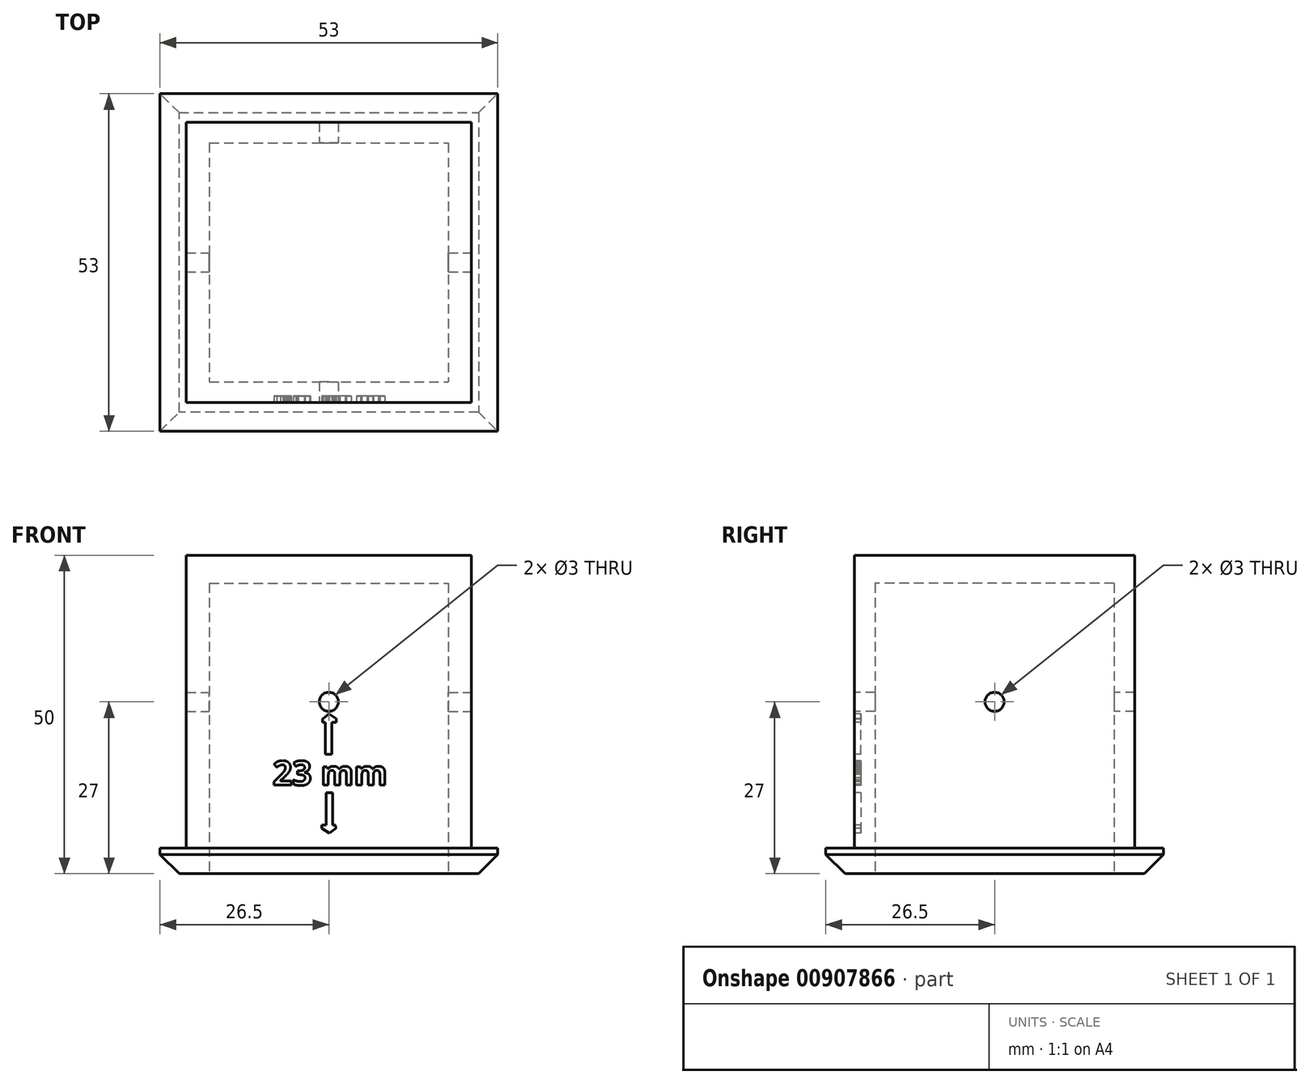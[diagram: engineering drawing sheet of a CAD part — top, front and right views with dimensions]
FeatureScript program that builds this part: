
annotation { "Feature Type Name" : "Feature", "Feature Type Description" : "" }
export const myFeature = defineFeature(function(context is Context, id is Id, definition is map)
    precondition{}
    {
        {
            var Q0;
            Q0=qCreatedBy(makeId("Top.planeOp"),FACE);
            var sketch = newSketch(context, id + "F0", { "sketchPlane" : qUnion([Q0])});
            skLineSegment(sketch, "E0.bottom", {"start": v(-18.75, 18.75) * mm, "end": v(18.75, 18.75) * mm});
            skLineSegment(sketch, "E0.top", {"start": v(-18.75, -18.75) * mm, "end": v(18.75, -18.75) * mm});
            skLineSegment(sketch, "E0.left", {"start": v(-18.75, 18.75) * mm, "end": v(-18.75, -18.75) * mm});
            skLineSegment(sketch, "E0.right", {"start": v(18.75, 18.75) * mm, "end": v(18.75, -18.75) * mm});
            skLineSegment(sketch, "E1.bottom", {"start": v(-22.4, 22) * mm, "end": v(22.4, 22) * mm});
            skLineSegment(sketch, "E1.top", {"start": v(-22.4, -22) * mm, "end": v(22.4, -22) * mm});
            skLineSegment(sketch, "E1.left", {"start": v(-22.4, 22) * mm, "end": v(-22.4, -22) * mm});
            skLineSegment(sketch, "E1.right", {"start": v(22.4, 22) * mm, "end": v(22.4, -22) * mm});
            skLineSegment(sketch, "E2", {"start": v(0, 18.75) * mm, "end": v(0, -18.75) * mm, "construction": true});
            skLineSegment(sketch, "E3", {"start": v(-18.75, 0) * mm, "end": v(18.75, 0) * mm, "construction": true});
            skLineSegment(sketch, "E4", {"start": v(0, 22) * mm, "end": v(0, -22) * mm, "construction": true});
            skLineSegment(sketch, "E5", {"start": v(-22.4, 0) * mm, "end": v(22.4, 0) * mm, "construction": true});
            skSolve(sketch);
        }
        {
            var Q0;
            Q0=makeQuery(id+"F0.imprint","IMPRINT",FACE,{"disambiguationData":[TD([[makeQuery(id+"F0.imprint","IMPRINT",EDGE,{"derivedFrom":sQuery(id+"F0.wireOp",EDGE,"E0.bottom")}),1.0]])]});
            var Q1;
            Q1=makeQuery(id+"F0.imprint","IMPRINT",FACE,{"disambiguationData":[TD([[makeQuery(id+"F0.imprint","IMPRINT",EDGE,{"derivedFrom":sQuery(id+"F0.wireOp",EDGE,"E0.bottom")}),-1.0]])]});
            extrude(context, id + "F1", {"entities" : qUnion([Q0, Q1]), "depth" : 50 * mm, "offsetDistance" : 25 * mm});
        }
        {
            var Q0;
            Q0=makeQuery(id+"F0.imprint","IMPRINT",FACE,{"disambiguationData":[TD([[makeQuery(id+"F0.imprint","IMPRINT",EDGE,{"derivedFrom":sQuery(id+"F0.wireOp",EDGE,"E0.bottom")}),-1.0]])]});
            extrude(context, id + "F2", {"entities" : qUnion([Q0]), "operationType" : NewBodyOperationType.REMOVE, "depth" : 45.6 * mm, "offsetDistance" : 25 * mm});
        }
        {
            var Q0;
            Q0=qCreatedBy(makeId("Top.planeOp"),FACE);
            cPlane(context, id + "F3", {"entities" : qUnion([Q0]), "cplaneType" : CPlaneType.OFFSET, "offset" : 4 * mm, "width" : 150 * mm, "height" : 150 * mm});
        }
        {
            var Q0;
            Q0=qCreatedBy(id+"F3.planeOp",FACE);
            var sketch = newSketch(context, id + "F4", { "sketchPlane" : qUnion([Q0])});
            skLineSegment(sketch, "E6", {"start": v(-21.08, -20.86) * mm, "end": v(-21.08, 21.6) * mm});
            skLineSegment(sketch, "E7", {"start": v(-21.08, 21.6) * mm, "end": v(21.57, 21.6) * mm});
            skLineSegment(sketch, "E8", {"start": v(21.57, 21.6) * mm, "end": v(21.57, -21.09) * mm});
            skLineSegment(sketch, "E9", {"start": v(21.57, -21.09) * mm, "end": v(-21.08, -20.86) * mm});
            skLineSegment(sketch, "E10.bottom", {"start": v(-26.5, -26.5) * mm, "end": v(26.5, -26.5) * mm});
            skLineSegment(sketch, "E10.top", {"start": v(-26.5, 26.5) * mm, "end": v(26.5, 26.5) * mm});
            skLineSegment(sketch, "E10.left", {"start": v(-26.5, -26.5) * mm, "end": v(-26.5, 26.5) * mm});
            skLineSegment(sketch, "E10.right", {"start": v(26.5, -26.5) * mm, "end": v(26.5, 26.5) * mm});
            skLineSegment(sketch, "E11", {"start": v(26.5, 0) * mm, "end": v(-26.5, 0) * mm, "construction": true});
            skLineSegment(sketch, "E12", {"start": v(0, -26.5) * mm, "end": v(0, 26.5) * mm, "construction": true});
            skSolve(sketch);
        }
        {
            var Q0;
            Q0=makeQuery(id+"F4.imprint","IMPRINT",FACE,{"disambiguationData":[TD([[makeQuery(id+"F4.imprint","IMPRINT",EDGE,{"derivedFrom":sQuery(id+"F4.wireOp",EDGE,"E6")}),1.0]])]});
            var Q1;
            Q1=makeQuery(id+"F1.opExtrude","CAP_FACE",FACE,{"disambiguationData":[OSD([sQuery(id+"F0.wireOp",EDGE,"E1.bottom"),sQuery(id+"F0.wireOp",EDGE,"E1.top"),sQuery(id+"F0.wireOp",EDGE,"E1.left"),sQuery(id+"F0.wireOp",EDGE,"E1.right")])],"isStart":true});
            extrude(context, id + "F5", {"entities" : qUnion([Q0]), "operationType" : NewBodyOperationType.ADD, "endBound" : BoundingType.UP_TO_SURFACE, "oppositeDirection" : true, "depth" : 3.67 * mm, "endBoundEntityFace" : qUnion([Q1]), "offsetDistance" : 25 * mm});
        }
        {
            var Q0;
            Q0=makeQuery(id+"F5.opExtrude","CAP_EDGE",EDGE,{"disambiguationData":[OSD([sQuery(id+"F4.wireOp",EDGE,"E10.top")])],"isStart":false});
            var Q1;
            Q1=makeQuery(id+"F5.opExtrude","CAP_EDGE",EDGE,{"disambiguationData":[OSD([sQuery(id+"F4.wireOp",EDGE,"E10.right")])],"isStart":false});
            var Q2;
            Q2=makeQuery(id+"F5.opExtrude","CAP_EDGE",EDGE,{"disambiguationData":[OSD([sQuery(id+"F4.wireOp",EDGE,"E10.left")])],"isStart":false});
            var Q3;
            Q3=makeQuery(id+"F5.opExtrude","CAP_EDGE",EDGE,{"disambiguationData":[OSD([sQuery(id+"F4.wireOp",EDGE,"E10.bottom")])],"isStart":false});
            chamfer(context, id + "F6", {"entities" : qUnion([Q0, Q1, Q2, Q3]), "width" : 3 * mm, "tangentPropagation" : true});
        }
        {
            var Q0;
            Q0=makeQuery(id+"F1.opExtrude","SWEPT_FACE",FACE,{"disambiguationData":[OSD([sQuery(id+"F0.wireOp",EDGE,"E1.right")])]});
            var sketch = newSketch(context, id + "F7", { "sketchPlane" : qUnion([Q0])});
            skCircle(sketch, "E13", {"center": v(0, 27) * mm, "radius": 1.5 * mm});
            skSolve(sketch);
        }
        {
            var Q0;
            Q0=makeQuery(id+"F7.imprint","IMPRINT",FACE,{"disambiguationData":[TD([[makeQuery(id+"F7.imprint","IMPRINT",EDGE,{"derivedFrom":sQuery(id+"F7.wireOp",EDGE,"E13")}),1.0]])]});
            var Q1;
            Q1=sQuery(id+"F7.wireOp",EDGE,"E13");
            var Q2;
            Q2=makeQuery(id+"F1.opExtrude","SWEPT_FACE",FACE,{"disambiguationData":[OSD([sQuery(id+"F0.wireOp",EDGE,"E1.left")])]});
            extrude(context, id + "F8", {"entities" : qUnion([Q0]), "operationType" : NewBodyOperationType.REMOVE, "surfaceEntities" : qUnion([Q1]), "endBound" : BoundingType.UP_TO_SURFACE, "oppositeDirection" : true, "depth" : 25 * mm, "endBoundEntityFace" : qUnion([Q2]), "offsetDistance" : 25 * mm});
        }
        {
            var Q0;
            Q0=makeQuery(id+"F1.opExtrude","SWEPT_FACE",FACE,{"disambiguationData":[OSD([sQuery(id+"F0.wireOp",EDGE,"E1.top")])]});
            var sketch = newSketch(context, id + "F9", { "sketchPlane" : qUnion([Q0])});
            skCircle(sketch, "E14", {"center": v(0, 27) * mm, "radius": 1.5 * mm});
            skSolve(sketch);
        }
        {
            var Q0;
            Q0=makeQuery(id+"F9.imprint","IMPRINT",FACE,{"disambiguationData":[TD([[makeQuery(id+"F9.imprint","IMPRINT",EDGE,{"derivedFrom":sQuery(id+"F9.wireOp",EDGE,"E14")}),1.0]])]});
            var Q1;
            Q1=sQuery(id+"F9.wireOp",EDGE,"E14");
            var Q2;
            Q2=makeQuery(id+"F1.opExtrude","SWEPT_FACE",FACE,{"disambiguationData":[OSD([sQuery(id+"F0.wireOp",EDGE,"E1.bottom")])]});
            extrude(context, id + "F10", {"entities" : qUnion([Q0]), "operationType" : NewBodyOperationType.REMOVE, "surfaceEntities" : qUnion([Q1]), "endBound" : BoundingType.UP_TO_SURFACE, "oppositeDirection" : true, "depth" : 25 * mm, "endBoundEntityFace" : qUnion([Q2]), "offsetDistance" : 25 * mm});
        }
        {
            var Q0;
            Q0=makeQuery(id+"F1.opExtrude","SWEPT_FACE",FACE,{"disambiguationData":[OSD([sQuery(id+"F0.wireOp",EDGE,"E1.top")])]});
            var sketch = newSketch(context, id + "F11", { "sketchPlane" : qUnion([Q0])});
            skText(sketch, "E15", { "text": "23 mm", "fontName": "OpenSans-Bold.ttf"});
            skLineSegment(sketch, "E16", {"start": v(-1, 24.3) * mm, "end": v(0, 25.1) * mm});
            skLineSegment(sketch, "E17", {"start": v(0, 25.1) * mm, "end": v(1.16, 24.32) * mm});
            skLineSegment(sketch, "E18", {"start": v(1.16, 24.32) * mm, "end": v(1.16, 23.8) * mm});
            skLineSegment(sketch, "E19", {"start": v(1.16, 23.8) * mm, "end": v(0.47, 23.8) * mm});
            skLineSegment(sketch, "E20", {"start": v(0.47, 23.8) * mm, "end": v(0.47, 18.75) * mm});
            skLineSegment(sketch, "E21", {"start": v(0.47, 18.75) * mm, "end": v(-0.54, 18.75) * mm});
            skLineSegment(sketch, "E22", {"start": v(-0.54, 18.75) * mm, "end": v(-0.54, 23.8) * mm});
            skLineSegment(sketch, "E23", {"start": v(-0.54, 23.8) * mm, "end": v(-0.98, 23.8) * mm});
            skLineSegment(sketch, "E24", {"start": v(-0.98, 23.8) * mm, "end": v(-1, 24.3) * mm});
            skLineSegment(sketch, "E25", {"start": v(1.07, 7.14) * mm, "end": v(0.06, 6.35) * mm});
            skLineSegment(sketch, "E26", {"start": v(0.06, 6.35) * mm, "end": v(-1.1, 7.12) * mm});
            skLineSegment(sketch, "E27", {"start": v(-1.1, 7.12) * mm, "end": v(-1.1, 7.65) * mm});
            skLineSegment(sketch, "E28", {"start": v(-1.1, 7.65) * mm, "end": v(-0.41, 7.65) * mm});
            skLineSegment(sketch, "E29", {"start": v(-0.41, 7.65) * mm, "end": v(-0.41, 12.7) * mm});
            skLineSegment(sketch, "E30", {"start": v(-0.41, 12.7) * mm, "end": v(0.6, 12.7) * mm});
            skLineSegment(sketch, "E31", {"start": v(0.6, 12.7) * mm, "end": v(0.6, 7.65) * mm});
            skLineSegment(sketch, "E32", {"start": v(0.6, 7.65) * mm, "end": v(1.04, 7.65) * mm});
            skLineSegment(sketch, "E33", {"start": v(1.04, 7.65) * mm, "end": v(1.07, 7.14) * mm});
            const initialGuessF11  = {"E15": [-0.0088, 0.0139, 1, 0, 0.00385]};
            skSetInitialGuess(sketch, initialGuessF11);
            skSolve(sketch);
        }
        {
            var Q0;
            Q0=makeQuery(id+"F11.imprint","IMPRINT",FACE,{"disambiguationData":[TD([[makeQuery(id+"F11.imprint","IMPRINT",EDGE,{"derivedFrom":sQuery(id+"F11.wireOp",EDGE,"E15.sketch_text.stroke-24")}),-1.0]])]});
            var Q1;
            Q1=makeQuery(id+"F11.imprint","IMPRINT",FACE,{"disambiguationData":[TD([[makeQuery(id+"F11.imprint","IMPRINT",EDGE,{"derivedFrom":sQuery(id+"F11.wireOp",EDGE,"E15.sketch_text.stroke-0")}),-1.0]])]});
            var Q2;
            Q2=makeQuery(id+"F11.imprint","IMPRINT",FACE,{"disambiguationData":[TD([[makeQuery(id+"F11.imprint","IMPRINT",EDGE,{"derivedFrom":sQuery(id+"F11.wireOp",EDGE,"E15.sketch_text.stroke-51")}),-1.0]])]});
            var Q3;
            Q3=makeQuery(id+"F11.imprint","IMPRINT",FACE,{"disambiguationData":[TD([[makeQuery(id+"F11.imprint","IMPRINT",EDGE,{"derivedFrom":sQuery(id+"F11.wireOp",EDGE,"E15.sketch_text.stroke-79")}),-1.0]])]});
            var Q4;
            Q4=makeQuery(id+"F11.imprint","IMPRINT",FACE,{"disambiguationData":[TD([[makeQuery(id+"F11.imprint","IMPRINT",EDGE,{"derivedFrom":sQuery(id+"F11.wireOp",EDGE,"E16")}),-1.0]])]});
            var Q5;
            Q5=makeQuery(id+"F11.imprint","IMPRINT",FACE,{"disambiguationData":[TD([[makeQuery(id+"F11.imprint","IMPRINT",EDGE,{"derivedFrom":sQuery(id+"F11.wireOp",EDGE,"E25")}),-1.0]])]});
            extrude(context, id + "F12", {"entities" : qUnion([Q0, Q1, Q2, Q3, Q4, Q5]), "operationType" : NewBodyOperationType.REMOVE, "oppositeDirection" : true, "depth" : 1 * mm, "offsetDistance" : 25 * mm});
        }
    });
